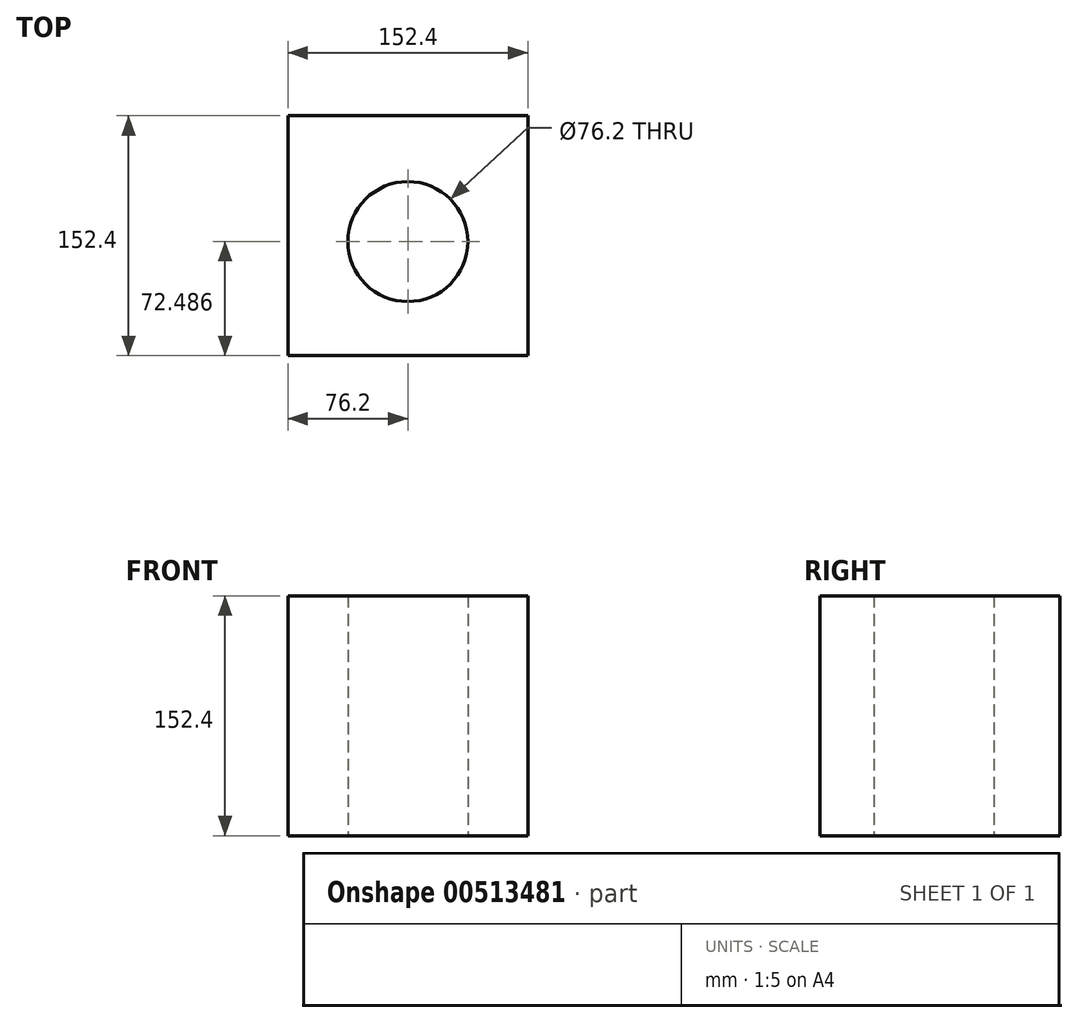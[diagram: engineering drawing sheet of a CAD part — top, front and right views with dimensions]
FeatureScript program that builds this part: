
annotation { "Feature Type Name" : "Feature", "Feature Type Description" : "" }
export const myFeature = defineFeature(function(context is Context, id is Id, definition is map)
    precondition{}
    {
        {
            var Q0;
            Q0=qCreatedBy(makeId("Top.planeOp"),FACE);
            var sketch = newSketch(context, id + "F0", { "sketchPlane" : qUnion([Q0])});
            skLineSegment(sketch, "E0.bottom", {"start": v(76.2, 76.2) * mm, "end": v(-76.2, 76.2) * mm});
            skLineSegment(sketch, "E0.top", {"start": v(76.2, -76.2) * mm, "end": v(-76.2, -76.2) * mm});
            skLineSegment(sketch, "E0.left", {"start": v(76.2, 76.2) * mm, "end": v(76.2, -76.2) * mm});
            skLineSegment(sketch, "E0.right", {"start": v(-76.2, 76.2) * mm, "end": v(-76.2, -76.2) * mm});
            skPoint(sketch, "E0.middle", {"position": v(0, 0) * mm});
            skCircle(sketch, "E1", {"center": v(0, -3.71) * mm, "radius": 38.1 * mm});
            skSolve(sketch);
        }
        {
            var Q0;
            Q0=makeQuery(id+"F0.imprint","IMPRINT",FACE,{"disambiguationData":[TD([[makeQuery(id+"F0.imprint","IMPRINT",EDGE,{"derivedFrom":sQuery(id+"F0.wireOp",EDGE,"E0.bottom")}),1.0]])]});
            extrude(context, id + "F1", {"entities" : qUnion([Q0]), "depth" : 152.4 * mm});
        }
    });
